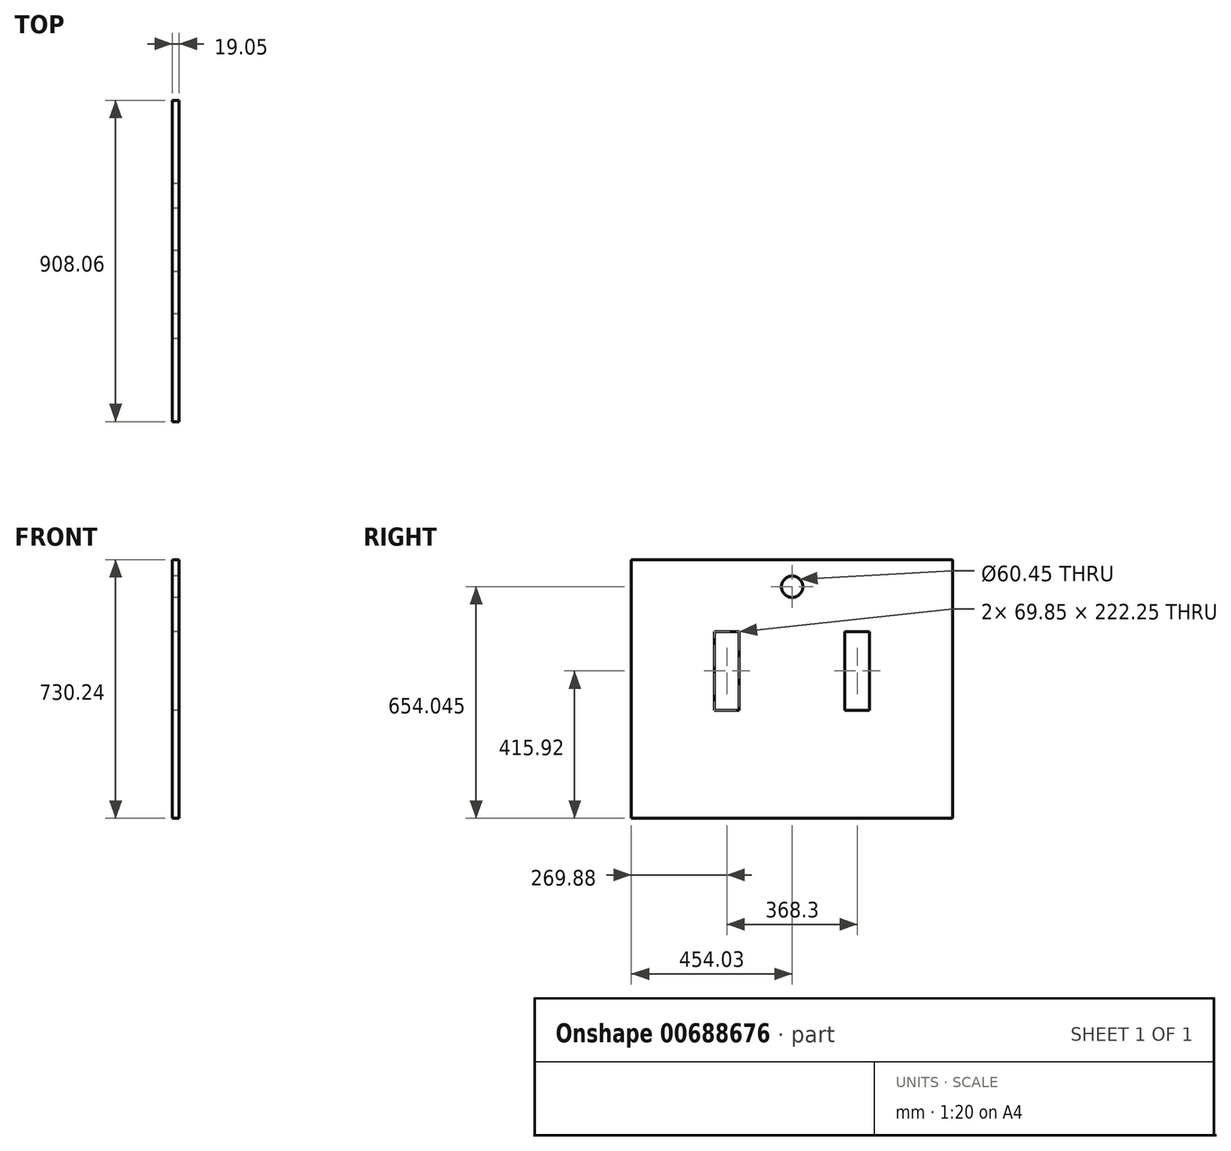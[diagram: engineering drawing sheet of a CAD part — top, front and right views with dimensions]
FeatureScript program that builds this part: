
annotation { "Feature Type Name" : "Feature", "Feature Type Description" : "" }
export const myFeature = defineFeature(function(context is Context, id is Id, definition is map)
    precondition{}
    {
        {
            var Q0;
            Q0=qCreatedBy(makeId("Right.planeOp"),FACE);
            var sketch = newSketch(context, id + "F0", { "sketchPlane" : qUnion([Q0])});
            skLineSegment(sketch, "E0.bottom", {"start": v(-454.02, 365.13) * mm, "end": v(454.02, 365.13) * mm});
            skLineSegment(sketch, "E0.top", {"start": v(-454.03, -365.12) * mm, "end": v(454.03, -365.12) * mm});
            skLineSegment(sketch, "E0.left", {"start": v(-454.02, 365.13) * mm, "end": v(-454.03, -365.12) * mm});
            skLineSegment(sketch, "E0.right", {"start": v(454.03, 365.13) * mm, "end": v(454.03, -365.12) * mm});
            skPoint(sketch, "E0.middle", {"position": v(0, 0) * mm});
            skLineSegment(sketch, "E1", {"start": v(0, 365.13) * mm, "end": v(0, 288.93) * mm});
            skCircle(sketch, "E2", {"center": v(0, 288.93) * mm, "radius": 30.23 * mm});
            skLineSegment(sketch, "E3", {"start": v(-454.03, -365.12) * mm, "end": v(-149.23, -365.12) * mm});
            skLineSegment(sketch, "E4", {"start": v(454.03, -365.12) * mm, "end": v(149.23, -365.12) * mm});
            skLineSegment(sketch, "E5", {"start": v(149.23, -365.13) * mm, "end": v(149.23, -60.32) * mm});
            skLineSegment(sketch, "E6", {"start": v(-149.23, -365.12) * mm, "end": v(-149.23, -60.32) * mm});
            skLineSegment(sketch, "E7.bottom", {"start": v(149.23, -60.32) * mm, "end": v(219.08, -60.32) * mm});
            skLineSegment(sketch, "E7.top", {"start": v(149.22, 161.93) * mm, "end": v(219.08, 161.93) * mm});
            skLineSegment(sketch, "E7.left", {"start": v(149.23, -60.32) * mm, "end": v(149.22, 161.93) * mm});
            skLineSegment(sketch, "E7.right", {"start": v(219.08, -60.32) * mm, "end": v(219.08, 161.93) * mm});
            skLineSegment(sketch, "E8.bottom", {"start": v(-149.23, -60.32) * mm, "end": v(-219.08, -60.32) * mm});
            skLineSegment(sketch, "E8.top", {"start": v(-149.23, 161.93) * mm, "end": v(-219.08, 161.93) * mm});
            skLineSegment(sketch, "E8.left", {"start": v(-149.23, -60.32) * mm, "end": v(-149.23, 161.93) * mm});
            skLineSegment(sketch, "E8.right", {"start": v(-219.08, -60.32) * mm, "end": v(-219.08, 161.93) * mm});
            skSolve(sketch);
        }
        {
            var Q0;
            Q0=makeQuery(id+"F0.imprint","IMPRINT",FACE,{"disambiguationData":[TD([[makeQuery(id+"F0.imprint","IMPRINT",EDGE,{"derivedFrom":sQuery(id+"F0.wireOp",EDGE,"E0.top")}),1.0]])]});
            extrude(context, id + "F1", {"entities" : qUnion([Q0]), "depth" : 19.05 * mm, "offsetDistance" : 25.4 * mm});
        }
    });
